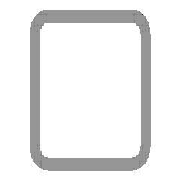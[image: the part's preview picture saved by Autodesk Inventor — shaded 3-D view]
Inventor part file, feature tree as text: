
AUTODESK INVENTOR PART (.ipt)
format: ipt  version: 2025.1 (Build 291241020, 241B)  size: 133,632 bytes
history: native  units: mm (DEFAULTED — no unit token found)
features: other x4, sketch x1, plane x1
ambient origin geometry x8: Origin, YZ Plane, XZ Plane, XY Plane, X Axis, Y Axis, Z Axis, Center Point
bodies: Solid1 (feature_tree), Body (feature_tree)
feature tree (6):
  parser-record x1  (decoder bookkeeping rows leaked as tree rows — omitted from the tree; the rows remain in map.json)
  other  "Driven Length"
  other  "Start Plane"
  other  "End Plane"
  sketch  "Sketch3"  dims[d3=660.0mm d4=0.0mm d7=4.0mm d9=40.0mm d11=40.0mm d12=2.0mm d13=50.0mm d14=710.0mm d15=20.0mm d16=20.0mm d17=90.0deg d18=660.0mm]
  plane  "Work Plane3"
